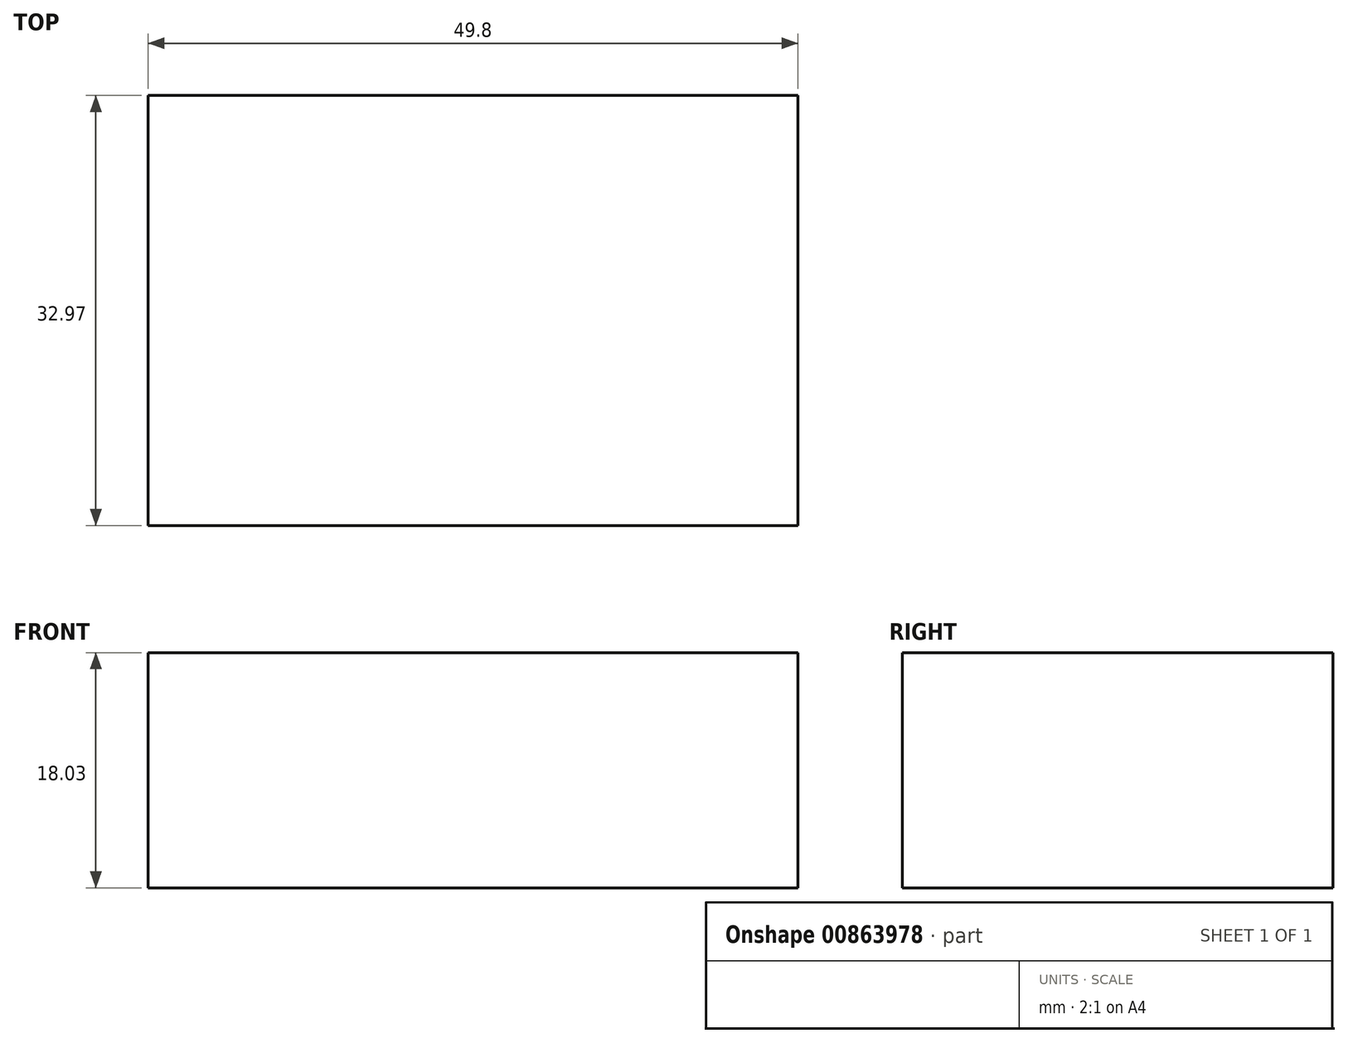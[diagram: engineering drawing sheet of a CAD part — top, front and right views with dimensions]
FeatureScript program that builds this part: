
annotation { "Feature Type Name" : "Feature", "Feature Type Description" : "" }
export const myFeature = defineFeature(function(context is Context, id is Id, definition is map)
    precondition{}
    {
        {
            var Q0;
            Q0=qCreatedBy(makeId("Top.planeOp"),FACE);
            var sketch = newSketch(context, id + "F0", { "sketchPlane" : qUnion([Q0])});
            skLineSegment(sketch, "E0.bottom", {"start": v(0, 0) * mm, "end": v(0, 0) * mm});
            skLineSegment(sketch, "E0.top", {"start": v(0, 32.97) * mm, "end": v(0, 32.97) * mm});
            skLineSegment(sketch, "E0.left", {"start": v(0, 0) * mm, "end": v(0, 32.97) * mm});
            skLineSegment(sketch, "E0.right", {"start": v(0, 0) * mm, "end": v(0, 32.97) * mm});
            skLineSegment(sketch, "E1.bottom", {"start": v(49.8, 32.97) * mm, "end": v(0, 32.97) * mm});
            skLineSegment(sketch, "E1.top", {"start": v(49.8, 0) * mm, "end": v(0, 0) * mm});
            skLineSegment(sketch, "E1.left", {"start": v(49.8, 32.97) * mm, "end": v(49.8, 0) * mm});
            skLineSegment(sketch, "E1.right", {"start": v(0, 32.97) * mm, "end": v(0, 0) * mm});
            skSolve(sketch);
        }
        {
            var Q0;
            Q0=makeQuery(id+"F0.imprint","IMPRINT",FACE,{"disambiguationData":[TD([[makeQuery(id+"F0.imprint","IMPRINT",EDGE,{"derivedFrom":sQuery(id+"F0.wireOp",EDGE,"E1.bottom")}),1.0]])]});
            extrude(context, id + "F1", {"entities" : qUnion([Q0]), "oppositeDirection" : true, "depth" : 18.03 * mm, "offsetDistance" : 25.4 * mm});
        }
    });
